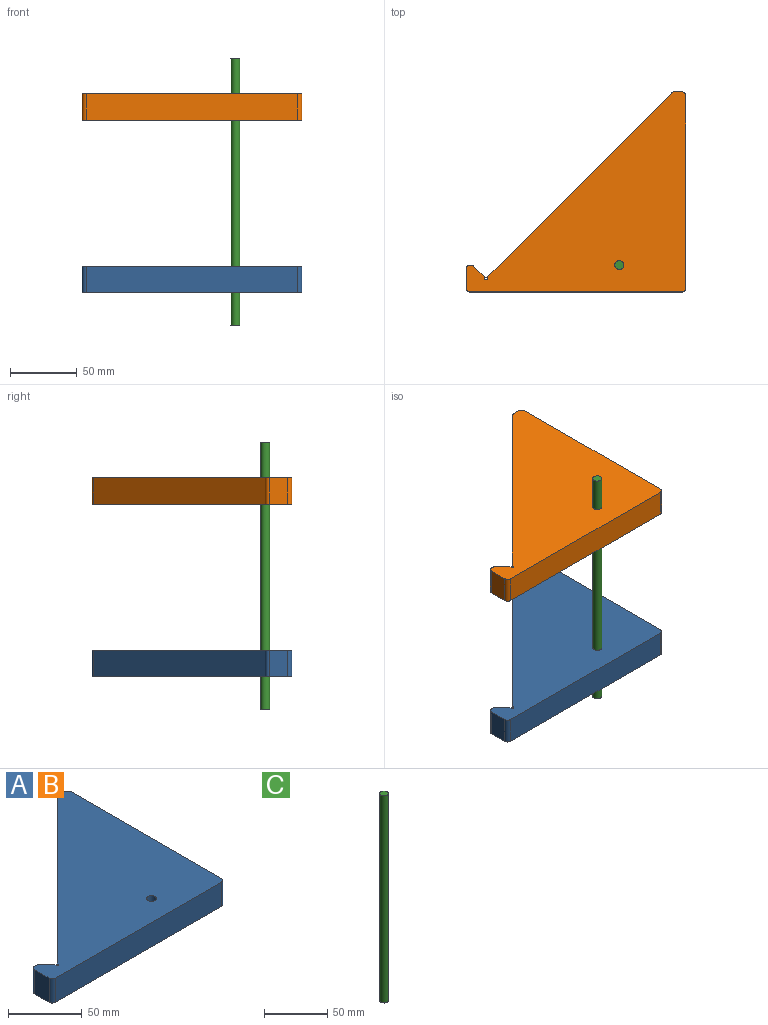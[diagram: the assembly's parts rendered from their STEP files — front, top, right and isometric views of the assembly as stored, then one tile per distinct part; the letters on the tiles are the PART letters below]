
ASSEMBLY  parts=3 mates=2
PART A: 17 faces, bbox 165x150x20 mm
  f0: plane 144x20mm, normal (1,0,0), area 2880mm2, adj f1,f13,f15,f16
  f1: cylinder r=3mm len=20mm, axis (0,0,-1), area 94.2mm2, adj f0,f2,f15,f16
  f2: plane 20x5.76mm, normal (0,1,0), area 115.1mm2, adj f1,f3,f15,f16
  f3: cylinder r=3mm len=20mm, axis (0,0,-1), area 47.1mm2, adj f2,f4,f15,f16
  f4: plane 138.41x138.41mm, normal (-0.71,0.71,0), area 3914.9mm2, adj f3,f5,f15,f16
  f5: cylinder r=1mm len=20mm, axis (0,0,-1), area 94.2mm2, adj f4,f6,f15,f16
  f6: plane 20x8.41mm, normal (0.71,0.71,0), area 238mm2, adj f5,f7,f15,f16
  f7: cylinder r=3mm len=20mm, axis (0,0,-1), area 47.1mm2, adj f6,f8,f15,f16
  f8: plane 20x0.76mm, normal (0,1,0), area 15.1mm2, adj f7,f9,f15,f16
  f9: cylinder r=3mm len=20mm, axis (0,0,-1), area 94.2mm2, adj f8,f10,f15,f16
  f10: plane 20x14mm, normal (-1,0,0), area 280mm2, adj f9,f11,f15,f16
  f11: cylinder r=3mm len=20mm, axis (0,0,-1), area 94.2mm2, adj f10,f12,f15,f16
  f12: plane 159x20mm, normal (0,-1,0), area 3180mm2, adj f11,f13,f15,f16
  f13: cylinder r=3mm len=20mm, axis (0,0,-1), area 94.2mm2, adj f0,f12,f15,f16
  f14: cylinder r=3.4mm len=20mm, axis (0,0,-1), area 427.3mm2, adj f15,f16
  f15: plane 165x150mm, normal (0,0,1), area 12903.2mm2, adj f0,f1,f2,f3,f4,f5,f6,f7
  f16: plane 165x150mm, normal (0,0,-1), area 12903.2mm2, adj f0,f1,f2,f3,f4,f5,f6,f7
PART B: same geometry as A
PART C: 3 faces, bbox 6.8x6.8x200 mm
  f0: cylinder r=3.4mm len=200mm, axis (0,0,-1), area 4272.6mm2, adj f1,f2
  f1: plane 6.8x6.8mm, normal (0,0,1), area 36.3mm2, adj f0
  f2: plane 6.8x6.8mm, normal (0,0,-1), area 36.3mm2, adj f0
PLACE A t=(49.77,30.4,-49.47)mm
PLACE B t=(49.77,30.4,79.88)mm
PLACE C t=(86.07,-22.41,-73.93)mm
MATE slider C.f0 <-> B.f14  axis (0,0,-1) through (86.07,-22.41,126.07)mm
MATE cylindrical C.f0 <-> A.f14  axis (0,0,-1) through (86.07,-22.41,-73.93)mm
